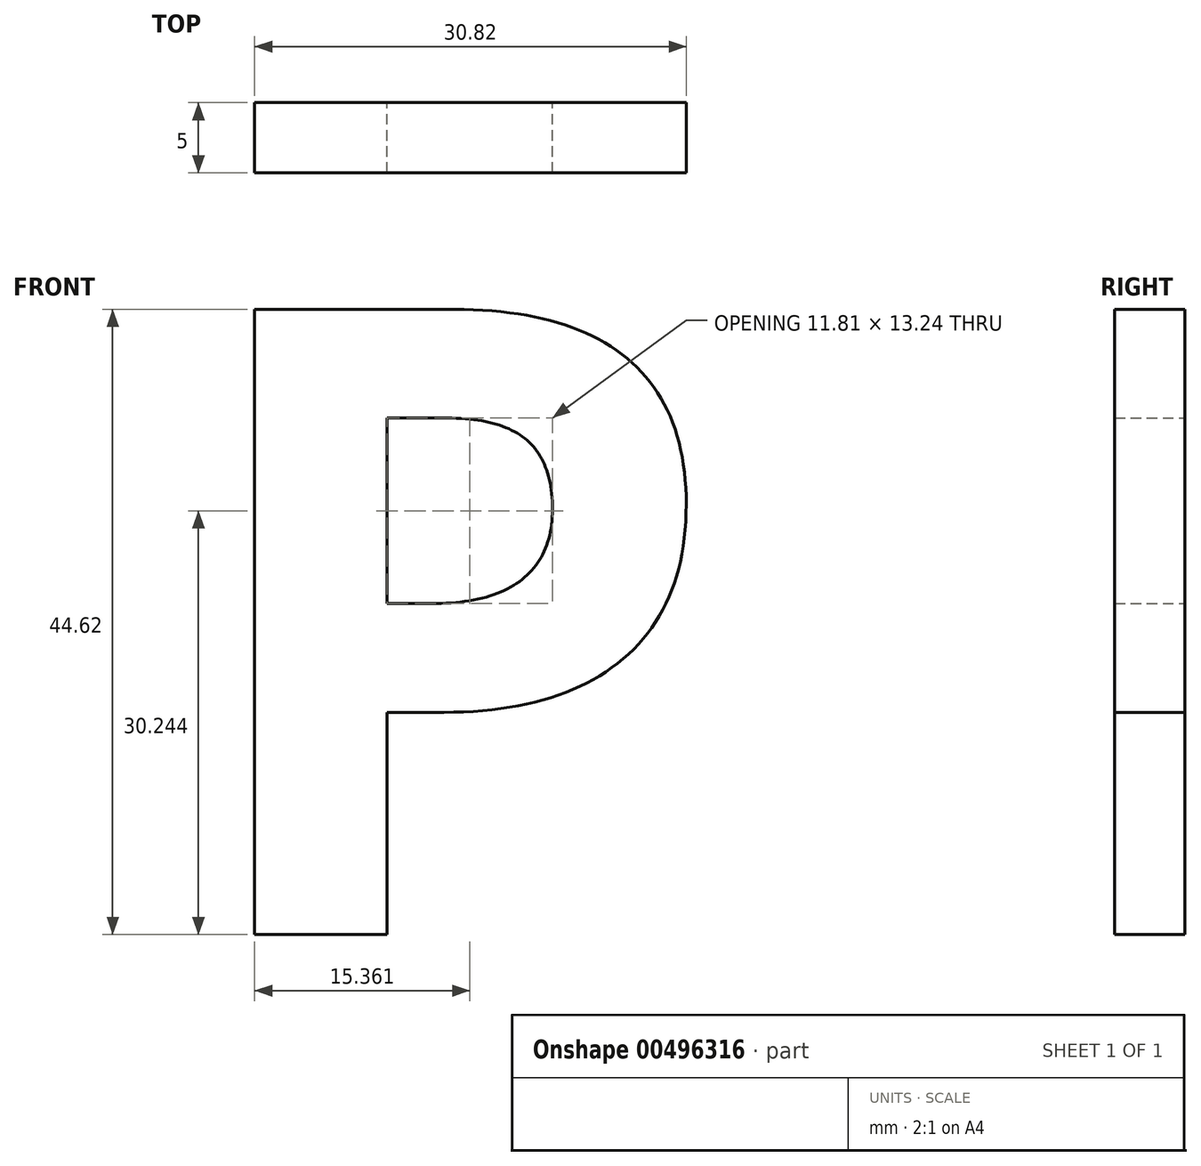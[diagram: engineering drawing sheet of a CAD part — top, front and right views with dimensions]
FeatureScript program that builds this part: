
annotation { "Feature Type Name" : "Feature", "Feature Type Description" : "" }
export const myFeature = defineFeature(function(context is Context, id is Id, definition is map)
    precondition{}
    {
        {
            var Q0;
            Q0=qCreatedBy(makeId("Front.planeOp"),FACE);
            var sketch = newSketch(context, id + "F0", { "sketchPlane" : qUnion([Q0])});
            skText(sketch, "E0", { "text": "P", "fontName": "OpenSans-Bold.ttf"});
            const initialGuessF0  = {"E0": [-0.08653, 0.03975, 1, 0, 0.045]};
            skSetInitialGuess(sketch, initialGuessF0);
            skSolve(sketch);
        }
        {
            var Q0;
            Q0=makeQuery(id+"F0.imprint","IMPRINT",FACE,{"disambiguationData":[TD([[makeQuery(id+"F0.imprint","IMPRINT",EDGE,{"derivedFrom":sQuery(id+"F0.wireOp",EDGE,"E0.sketch_text.stroke-0")}),-1.0]])]});
            extrude(context, id + "F1", {"entities" : qUnion([Q0]), "depth" : 5 * mm});
        }
    });
